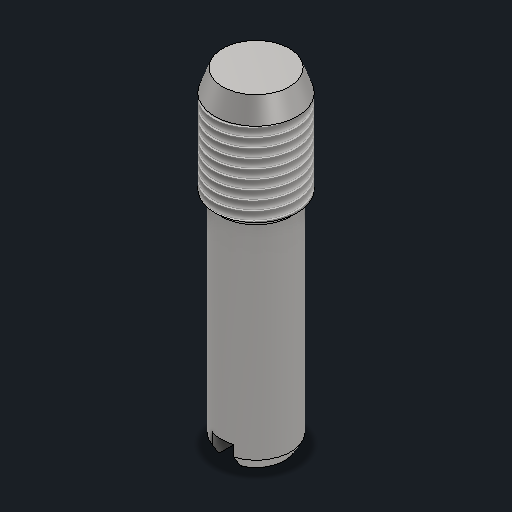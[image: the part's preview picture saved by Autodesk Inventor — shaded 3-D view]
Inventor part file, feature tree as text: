
AUTODESK INVENTOR PART (.ipt)
format: ipt  version: 2025.1 (Build 291241020, 241B)  size: 141,312 bytes
history: native  units: in
note: dims shown in document units (in); Inventor stores cm internally (conversion verified against a paired STEP export)
features: extrude x3, chamfer x3, sketch x2, thread x1, other x1
ambient origin geometry x8: Origin, YZ Plane, XZ Plane, XY Plane, X Axis, Y Axis, Z Axis, Center Point
bodies: Solid1 (feature_tree)
feature tree (10):
  sketch  "Sketch1"  dims[d0=0.16in d1=0.51in d2=0.0in]
  extrude  "Extrusion1"  Depth=0.51in TaperAngle=0.0deg
  extrude  "Extrusion2"  Depth=0.05in TaperAngle=0.0deg
  thread  "Thread2"  [1 undecoded]
  chamfer  "Chamfer1"  Distance=0.05in
  chamfer  "Chamfer2"  Distance=0.05in
  chamfer  "Chamfer3"  Distance=0.015in Angle=45.0deg
  extrude  "Extrusion3"  Depth=0.05in
  sketch  "Sketch2"  dims[d5=0.19in d6=0.2425in d7=0.0in d8=0.753in d9=0.0in d10=0.05in d11=0.05in d12=0.0in d13=0.015in d14=0.125in d15=45.0deg d16=0.05in d17=0.125in d18=0.1374in d19=0.025in d20=0.125in d21=30.0deg]
  other  "Finish1"
note: 1 required parameter value undecoded (feature->parameter linkage not recoverable at this tier; creation-order binding heuristic only, values carry confidence <= 0.55)
